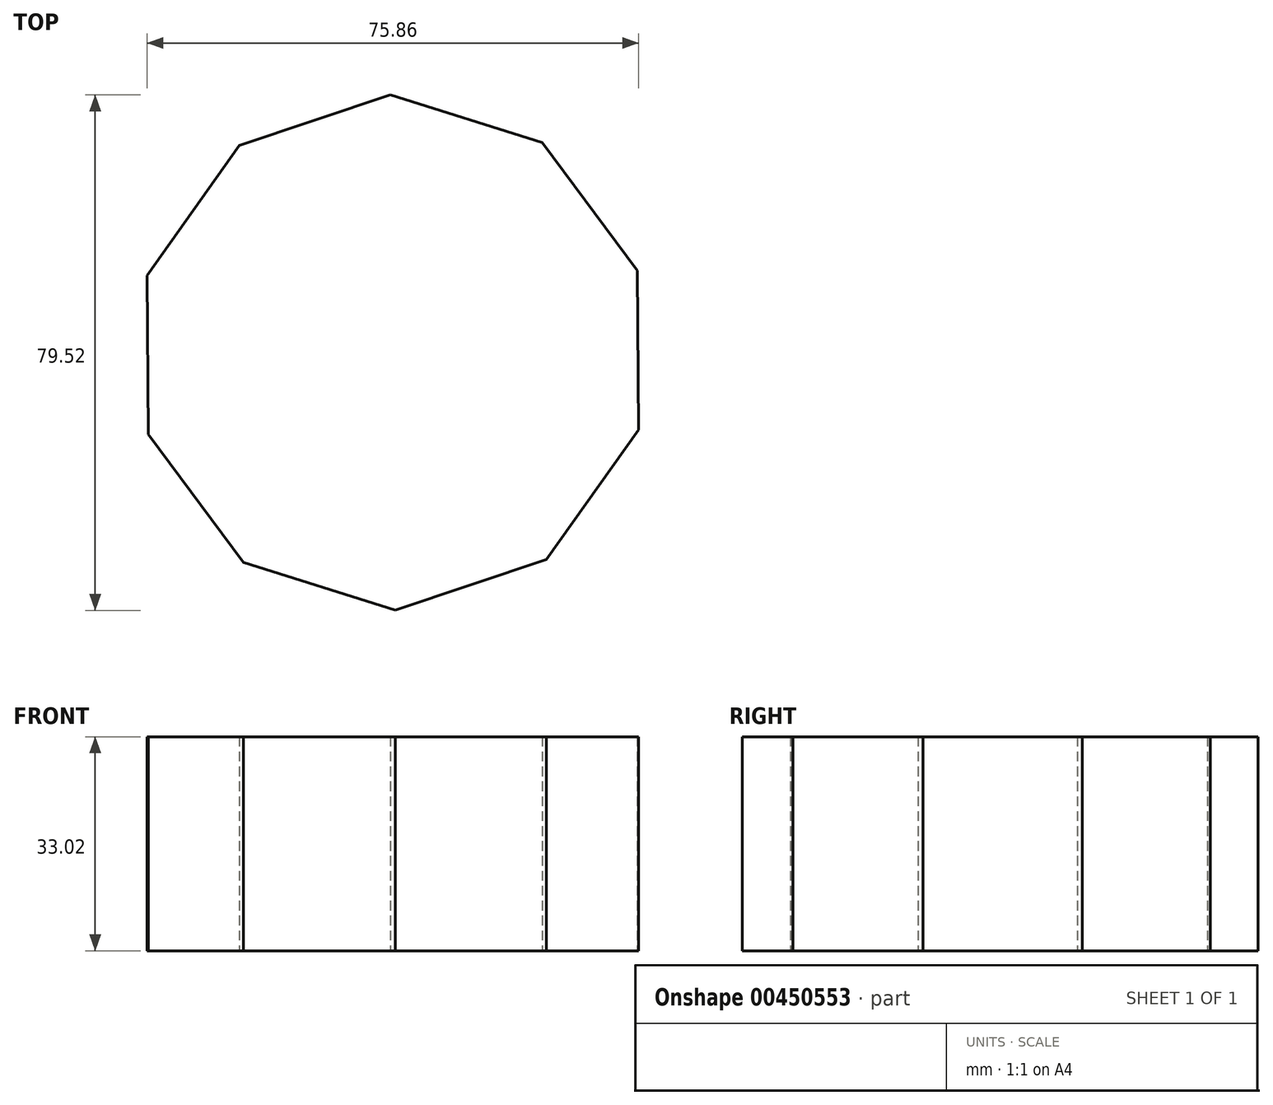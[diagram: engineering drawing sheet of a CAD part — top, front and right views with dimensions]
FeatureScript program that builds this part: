
annotation { "Feature Type Name" : "Feature", "Feature Type Description" : "" }
export const myFeature = defineFeature(function(context is Context, id is Id, definition is map)
    precondition{}
    {
        {
            var Q0;
            Q0=qCreatedBy(makeId("Top.planeOp"),FACE);
            var sketch = newSketch(context, id + "F0", { "sketchPlane" : qUnion([Q0])});
            skCircle(sketch, "E0.cCircle", {"center": v(0, 0) * mm, "radius": 37.81 * mm, "construction": true});
            skLineSegment(sketch, "E0.0", {"start": v(-23.67, 31.94) * mm, "end": v(-0.37, 39.76) * mm});
            skLineSegment(sketch, "E0.1", {"start": v(-0.37, 39.76) * mm, "end": v(23.07, 32.39) * mm});
            skLineSegment(sketch, "E0.2", {"start": v(23.07, 32.39) * mm, "end": v(37.7, 12.64) * mm});
            skLineSegment(sketch, "E0.3", {"start": v(37.7, 12.64) * mm, "end": v(37.93, -11.93) * mm});
            skLineSegment(sketch, "E0.4", {"start": v(37.93, -11.93) * mm, "end": v(23.67, -31.94) * mm});
            skLineSegment(sketch, "E0.5", {"start": v(23.67, -31.94) * mm, "end": v(0.37, -39.76) * mm});
            skLineSegment(sketch, "E0.6", {"start": v(0.37, -39.76) * mm, "end": v(-23.07, -32.39) * mm});
            skLineSegment(sketch, "E0.7", {"start": v(-23.07, -32.39) * mm, "end": v(-37.7, -12.64) * mm});
            skLineSegment(sketch, "E0.8", {"start": v(-37.7, -12.64) * mm, "end": v(-37.93, 11.93) * mm});
            skLineSegment(sketch, "E0.9", {"start": v(-37.93, 11.93) * mm, "end": v(-23.67, 31.94) * mm});
            skPoint(sketch, "E0.0.midPoint", {"position": v(-12.02, 35.85) * mm});
            skSolve(sketch);
        }
        {
            var Q0;
            Q0 = qSketchRegion(id + "F0", true);
            extrude(context, id + "F1", {"entities" : qUnion([Q0]), "depth" : 7.62 * mm});
        }
        {
            var Q0;
            Q0=makeQuery(id+"F1.opExtrude","CAP_FACE",FACE,{"disambiguationData":[OSD([sQuery(id+"F0.wireOp",EDGE,"E0.0"),sQuery(id+"F0.wireOp",EDGE,"E0.1"),sQuery(id+"F0.wireOp",EDGE,"E0.2"),sQuery(id+"F0.wireOp",EDGE,"E0.3"),sQuery(id+"F0.wireOp",EDGE,"E0.4"),sQuery(id+"F0.wireOp",EDGE,"E0.5"),sQuery(id+"F0.wireOp",EDGE,"E0.6"),sQuery(id+"F0.wireOp",EDGE,"E0.7"),sQuery(id+"F0.wireOp",EDGE,"E0.8"),sQuery(id+"F0.wireOp",EDGE,"E0.9")])],"isStart":false});
            extrude(context, id + "F2", {"entities" : qUnion([Q0]), "operationType" : NewBodyOperationType.ADD, "depth" : 25.4 * mm});
        }
    });
